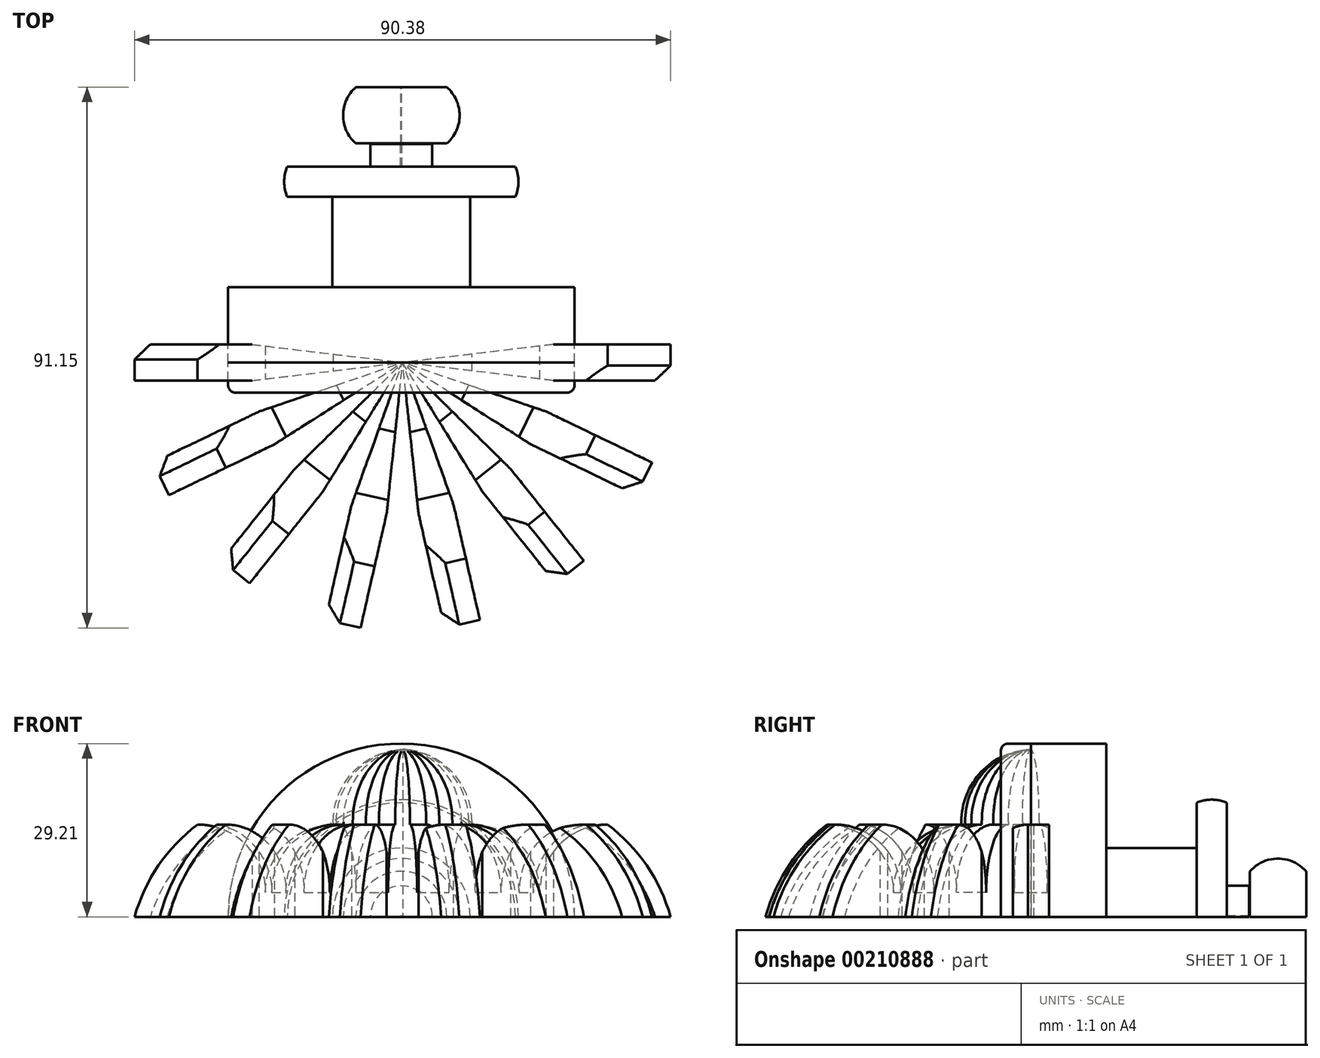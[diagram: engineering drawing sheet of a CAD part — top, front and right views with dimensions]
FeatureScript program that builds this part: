
annotation { "Feature Type Name" : "Feature", "Feature Type Description" : "" }
export const myFeature = defineFeature(function(context is Context, id is Id, definition is map)
    precondition{}
    {
        {
            var Q0;
            Q0=qCreatedBy(makeId("Front.planeOp"),FACE);
            var sketch = newSketch(context, id + "F0", { "sketchPlane" : qUnion([Q0])});
            skLineSegment(sketch, "E0.bottom", {"start": v(0.21, 15.56) * mm, "end": v(11.92, 15.56) * mm});
            skLineSegment(sketch, "E0.top", {"start": v(0.21, 0) * mm, "end": v(23.35, 0) * mm});
            skLineSegment(sketch, "E0.left", {"start": v(0.21, 15.56) * mm, "end": v(0.21, 0) * mm});
            skLineSegment(sketch, "E0.right", {"start": v(23.35, 4.13) * mm, "end": v(23.35, 0) * mm});
            skPoint(sketch, "E1.visualSharp", {"position": v(23.35, 15.56) * mm});
            skArc(sketch, "E1.filletArc", {"start": v(23.35, 4.13) * mm, "mid": v(20, 12.2) * mm, "end": v(11.92, 15.56) * mm});
            skLineSegment(sketch, "E2.MirrorCS", {"start": v(46.5, 15.56) * mm, "end": v(46.5, 0) * mm});
            skLineSegment(sketch, "E3.MirrorCS", {"start": v(46.5, 15.56) * mm, "end": v(34.78, 15.56) * mm});
            skArc(sketch, "E4.MirrorCS", {"start": v(23.35, 4.13) * mm, "mid": v(26.7, 12.2) * mm, "end": v(34.78, 15.56) * mm});
            skLineSegment(sketch, "E5.MirrorCS", {"start": v(46.5, 0) * mm, "end": v(23.35, 0) * mm});
            skSolve(sketch);
        }
        {
            var Q0;
            Q0=makeQuery(id+"F0.imprint","IMPRINT",FACE,{"disambiguationData":[TD([[makeQuery(id+"F0.imprint","IMPRINT",EDGE,{"derivedFrom":sQuery(id+"F0.wireOp",EDGE,"E0.bottom")}),-1.0]])]});
            var Q1;
            Q1=makeQuery(id+"F0.imprint","IMPRINT",FACE,{"disambiguationData":[TD([[makeQuery(id+"F0.imprint","IMPRINT",EDGE,{"derivedFrom":sQuery(id+"F0.wireOp",EDGE,"E0.right")}),1.0]])]});
            extrude(context, id + "F1", {"entities" : qUnion([Q0, Q1]), "endBound" : BoundingType.SYMMETRIC, "depth" : 6.1 * mm});
        }
        {
            var Q0;
            Q0=makeQuery(id+"F1.opExtrude","SWEPT_EDGE",EDGE,{"disambiguationData":[OSD([sQuery(id+"F0.wireOp",EDGE,"E2.MirrorCS"),sQuery(id+"F0.wireOp",EDGE,"E3.MirrorCS")])]});
            fillet(context, id + "F2", {"entities" : qUnion([Q0]), "radius" : 29.43 * mm, "tangentPropagation" : true, "allowEdgeOverflow" : false});
        }
        {
            var Q0;
            {var subQ0=sQuery(id+"F0.wireOp",EDGE,"E3.MirrorCS");var subQ1=sQuery(id+"F0.wireOp",EDGE,"E2.MirrorCS");Q0=makeQuery(id+"F2.opFillet","BLEND_EDGE",EDGE,{"blendedFrom":[makeQuery(id+"F1.opExtrude","SWEPT_EDGE",EDGE,{"disambiguationData":[OSD([subQ1,subQ0])]}),makeQuery(id+"F1.opExtrude","CAP_FACE",FACE,{"disambiguationData":[OSD([sQuery(id+"F0.wireOp",EDGE,"E0.bottom"),sQuery(id+"F0.wireOp",EDGE,"E0.top"),sQuery(id+"F0.wireOp",EDGE,"E0.left"),sQuery(id+"F0.wireOp",EDGE,"E1.filletArc"),subQ1,subQ0,sQuery(id+"F0.wireOp",EDGE,"E4.MirrorCS"),sQuery(id+"F0.wireOp",EDGE,"E5.MirrorCS")])],"isStart":false})],"blendedInto":[makeQuery(id+"F1.opExtrude","CAP_FACE",FACE,{"disambiguationData":[OSD([sQuery(id+"F0.wireOp",EDGE,"E0.bottom"),sQuery(id+"F0.wireOp",EDGE,"E0.top"),sQuery(id+"F0.wireOp",EDGE,"E0.left"),sQuery(id+"F0.wireOp",EDGE,"E1.filletArc"),subQ1,subQ0,sQuery(id+"F0.wireOp",EDGE,"E4.MirrorCS"),sQuery(id+"F0.wireOp",EDGE,"E5.MirrorCS")])],"isStart":false})]});}
            chamfer(context, id + "F3", {"entities" : qUnion([Q0]), "width" : 2.54 * mm, "tangentPropagation" : true});
        }
        {
            var Q0;
            Q0=makeQuery(id+"F1.opExtrude","SWEPT_FACE",FACE,{"disambiguationData":[OSD([sQuery(id+"F0.wireOp",EDGE,"E0.bottom")])]});
            extrude(context, id + "F4", {"entities" : qUnion([Q0]), "operationType" : NewBodyOperationType.ADD, "depth" : 12.7 * mm});
        }
        {
            var Q0;
            Q0=makeQuery(id+"F4.opExtrude","CAP_EDGE",EDGE,{"disambiguationData":[OSD([sQuery(id+"F0.wireOp",EDGE,"E0.bottom"),sQuery(id+"F0.wireOp",EDGE,"E1.filletArc")])],"isStart":false});
            fillet(context, id + "F5", {"entities" : qUnion([Q0]), "radius" : 12.26 * mm, "tangentPropagation" : true, "allowEdgeOverflow" : false});
        }
        {
            var Q0;
            {var subQ0=sQuery(id+"F0.wireOp",EDGE,"E0.left");var subQ1=sQuery(id+"F0.wireOp",EDGE,"E0.bottom");Q0=makeQuery(id+"F4.boolean.opBoolean","MERGE",EDGE,{"derivedFrom":[makeQuery(id+"F1.opExtrude","CAP_EDGE",EDGE,{"disambiguationData":[OSD([subQ0])],"isStart":true}),makeQuery(id+"F4.opExtrude","SWEPT_EDGE",EDGE,{"disambiguationData":[OSD([subQ1,subQ0]),TDD([makeQuery(id+"F1.opExtrude","CAP_VERTEX",VERTEX,{"disambiguationData":[OSD([subQ1,subQ0])],"isStart":true})])]})]});}
            var Q1;
            {var subQ0=sQuery(id+"F0.wireOp",EDGE,"E0.left");var subQ1=sQuery(id+"F0.wireOp",EDGE,"E0.bottom");Q1=makeQuery(id+"F4.boolean.opBoolean","MERGE",EDGE,{"derivedFrom":[makeQuery(id+"F1.opExtrude","CAP_EDGE",EDGE,{"disambiguationData":[OSD([subQ0])],"isStart":false}),makeQuery(id+"F4.opExtrude","SWEPT_EDGE",EDGE,{"disambiguationData":[OSD([subQ1,subQ0]),TDD([makeQuery(id+"F1.opExtrude","CAP_VERTEX",VERTEX,{"disambiguationData":[OSD([subQ1,subQ0])],"isStart":false})])]})]});}
            chamfer(context, id + "F6", {"entities" : qUnion([Q0, Q1]), "chamferType" : ChamferType.TWO_OFFSETS, "width1" : 3.05 * mm, "oppositeDirection" : false, "width2" : 25.4 * mm, "tangentPropagation" : true});
        }
        {
            var Q0;
            Q0=makeQuery(id+"F1.opExtrude","SWEPT_BODY",BODY,{"disambiguationData":[OSD([sQuery(id+"F0.wireOp",EDGE,"E0.bottom"),sQuery(id+"F0.wireOp",EDGE,"E0.top"),sQuery(id+"F0.wireOp",EDGE,"E0.left"),sQuery(id+"F0.wireOp",EDGE,"E1.filletArc"),sQuery(id+"F0.wireOp",EDGE,"E2.MirrorCS"),sQuery(id+"F0.wireOp",EDGE,"E3.MirrorCS"),sQuery(id+"F0.wireOp",EDGE,"E4.MirrorCS"),sQuery(id+"F0.wireOp",EDGE,"E5.MirrorCS")])]});
            var Q1;
            {var subQ0=sQuery(id+"F0.wireOp",EDGE,"E0.left");var subQ1=sQuery(id+"F0.wireOp",EDGE,"E0.bottom");Q1=makeQuery(id+"F6.opChamfer","BLEND_EDGE",EDGE,{"blendedFrom":[makeQuery(id+"F4.boolean.opBoolean","MERGE",EDGE,{"derivedFrom":[makeQuery(id+"F1.opExtrude","CAP_EDGE",EDGE,{"disambiguationData":[OSD([subQ0])],"isStart":true}),makeQuery(id+"F4.opExtrude","SWEPT_EDGE",EDGE,{"disambiguationData":[OSD([subQ1,subQ0]),TDD([makeQuery(id+"F1.opExtrude","CAP_VERTEX",VERTEX,{"disambiguationData":[OSD([subQ1,subQ0])],"isStart":true})])]})]}),makeQuery(id+"F4.boolean.opBoolean","MERGE",EDGE,{"derivedFrom":[makeQuery(id+"F1.opExtrude","CAP_EDGE",EDGE,{"disambiguationData":[OSD([subQ0])],"isStart":false}),makeQuery(id+"F4.opExtrude","SWEPT_EDGE",EDGE,{"disambiguationData":[OSD([subQ1,subQ0]),TDD([makeQuery(id+"F1.opExtrude","CAP_VERTEX",VERTEX,{"disambiguationData":[OSD([subQ1,subQ0])],"isStart":false})])]})]})],"blendedInto":[]});}
            circularPattern(context, id + "F7", {"entities" : qUnion([Q0]), "axis" : qUnion([Q1]), "angle" : 180 * degree, "instanceCount" : 8, "equalSpace" : true});
        }
        {
            var Q0;
            Q0=qCreatedBy(makeId("Right.planeOp"),FACE);
            var sketch = newSketch(context, id + "F8", { "sketchPlane" : qUnion([Q0])});
            skLineSegment(sketch, "E6.bottom", {"start": v(0, 29.21) * mm, "end": v(12.7, 29.21) * mm});
            skLineSegment(sketch, "E6.top", {"start": v(0, 0) * mm, "end": v(12.7, 0) * mm});
            skLineSegment(sketch, "E6.left", {"start": v(0, 29.2) * mm, "end": v(0, 0) * mm});
            skLineSegment(sketch, "E6.right", {"start": v(12.7, 29.2) * mm, "end": v(12.7, 0) * mm});
            skLineSegment(sketch, "E7.bottom", {"start": v(27.94, 11.6) * mm, "end": v(12.7, 11.6) * mm});
            skLineSegment(sketch, "E7.top", {"start": v(27.94, 0) * mm, "end": v(12.7, 0) * mm});
            skLineSegment(sketch, "E7.left", {"start": v(27.94, 11.6) * mm, "end": v(27.94, 0) * mm});
            skLineSegment(sketch, "E7.right", {"start": v(12.7, 11.6) * mm, "end": v(12.7, 0) * mm});
            skLineSegment(sketch, "E8.bottom", {"start": v(27.94, 0) * mm, "end": v(33.02, 0) * mm});
            skLineSegment(sketch, "E8.top", {"start": v(27.94, 19.23) * mm, "end": v(33.02, 19.23) * mm});
            skLineSegment(sketch, "E8.left", {"start": v(27.94, 0) * mm, "end": v(27.94, 19.23) * mm});
            skLineSegment(sketch, "E8.right", {"start": v(33.02, 0) * mm, "end": v(33.02, 19.23) * mm});
            skArc(sketch, "E9", {"start": v(33.02, 19.23) * mm, "mid": v(30.48, 19.76) * mm, "end": v(27.94, 19.23) * mm});
            skLineSegment(sketch, "E10.bottom", {"start": v(36.92, 0.05) * mm, "end": v(46.41, 0.05) * mm});
            skLineSegment(sketch, "E10.top", {"start": v(36.92, 7.67) * mm, "end": v(46.41, 7.67) * mm});
            skLineSegment(sketch, "E10.left", {"start": v(36.92, 0.05) * mm, "end": v(36.92, 7.67) * mm});
            skLineSegment(sketch, "E10.right", {"start": v(46.41, 0.05) * mm, "end": v(46.41, 7.67) * mm});
            skArc(sketch, "E11", {"start": v(46.41, 7.67) * mm, "mid": v(41.67, 9.82) * mm, "end": v(36.92, 7.67) * mm});
            skLineSegment(sketch, "E12.bottom", {"start": v(33, 0.14) * mm, "end": v(36.8, 0.14) * mm});
            skLineSegment(sketch, "E12.top", {"start": v(33, 5.22) * mm, "end": v(36.8, 5.22) * mm});
            skLineSegment(sketch, "E12.left", {"start": v(36.8, 0.14) * mm, "end": v(36.8, 5.22) * mm});
            skLineSegment(sketch, "E12.right", {"start": v(33, 0.14) * mm, "end": v(33, 5.22) * mm});
            skSolve(sketch);
        }
        {
            var Q0;
            Q0=makeQuery(id+"F8.imprint","IMPRINT",FACE,{"disambiguationData":[TD([[makeQuery(id+"F8.imprint","IMPRINT",EDGE,{"derivedFrom":sQuery(id+"F8.wireOp",EDGE,"E6.bottom")}),-1.0]])]});
            var Q1;
            {var subQ0=sQuery(id+"F8.wireOp",EDGE,"E7.bottom");Q1=makeQuery(id+"F8.imprint","IMPRINT",FACE,{"disambiguationData":[TD([[makeQuery(id+"F8.imprint","IMPRINT",EDGE,{"derivedFrom":subQ0}),1.0]])]});}
            var Q2;
            {var subQ2=sQuery(id+"F8.wireOp",EDGE,"E8.bottom");Q2=makeQuery(id+"F8.imprint","IMPRINT",FACE,{"disambiguationData":[TD([[makeQuery(id+"F8.imprint","IMPRINT",EDGE,{"derivedFrom":subQ2}),1.0]])]});}
            var Q3;
            Q3=makeQuery(id+"F8.imprint","IMPRINT",FACE,{"disambiguationData":[TD([[makeQuery(id+"F8.imprint","IMPRINT",EDGE,{"derivedFrom":sQuery(id+"F8.wireOp",EDGE,"E8.top")}),1.0]])]});
            var Q4;
            Q4=makeQuery(id+"F8.imprint","IMPRINT",FACE,{"disambiguationData":[TD([[makeQuery(id+"F8.imprint","IMPRINT",EDGE,{"derivedFrom":sQuery(id+"F8.wireOp",EDGE,"E12.bottom")}),1.0]])]});
            var Q5;
            Q5=makeQuery(id+"F8.imprint","IMPRINT",FACE,{"disambiguationData":[TD([[makeQuery(id+"F8.imprint","IMPRINT",EDGE,{"derivedFrom":sQuery(id+"F8.wireOp",EDGE,"E10.bottom")}),1.0]])]});
            var Q6;
            Q6=makeQuery(id+"F8.imprint","IMPRINT",FACE,{"disambiguationData":[TD([[makeQuery(id+"F8.imprint","IMPRINT",EDGE,{"derivedFrom":sQuery(id+"F8.wireOp",EDGE,"E10.top")}),1.0]])]});
            var Q7;
            Q7=sQuery(id+"F8.wireOp",EDGE,"E6.top");
            revolve(context, id + "F9", {"entities" : qUnion([Q0, Q1, Q2, Q3, Q4, Q5, Q6]), "axis" : qUnion([Q7]), "revolveType" : RevolveType.SYMMETRIC, "angle" : 180 * degree});
        }
        {
            var Q0;
            Q0=makeQuery(id+"F9.opRevolve","SWEPT_FACE",FACE,{"disambiguationData":[OSD([sQuery(id+"F8.wireOp",EDGE,"E6.left")])]});
            extrude(context, id + "F10", {"entities" : qUnion([Q0]), "depth" : 5.08 * mm});
        }
        {
            var Q0;
            Q0=makeQuery(id+"F10.opExtrude","CAP_EDGE",EDGE,{"disambiguationData":[OSD([sQuery(id+"F8.wireOp",EDGE,"E6.bottom"),sQuery(id+"F8.wireOp",EDGE,"E6.left")])],"isStart":false});
            fillet(context, id + "F11", {"entities" : qUnion([Q0]), "radius" : 1.27 * mm, "tangentPropagation" : true, "allowEdgeOverflow" : false});
        }
        {
            var Q0;
            Q0=makeQuery(id+"F8.imprint","IMPRINT",FACE,{"disambiguationData":[TD([[makeQuery(id+"F8.imprint","IMPRINT",EDGE,{"derivedFrom":sQuery(id+"F8.wireOp",EDGE,"E7.bottom")}),1.0]])]});
            var Q1;
            Q1=sQuery(id+"F8.wireOp",EDGE,"E7.top");
            revolve(context, id + "F12", {"operationType" : NewBodyOperationType.ADD, "entities" : qUnion([Q0]), "axis" : qUnion([Q1]), "revolveType" : RevolveType.SYMMETRIC, "angle" : 180 * degree});
        }
    });
